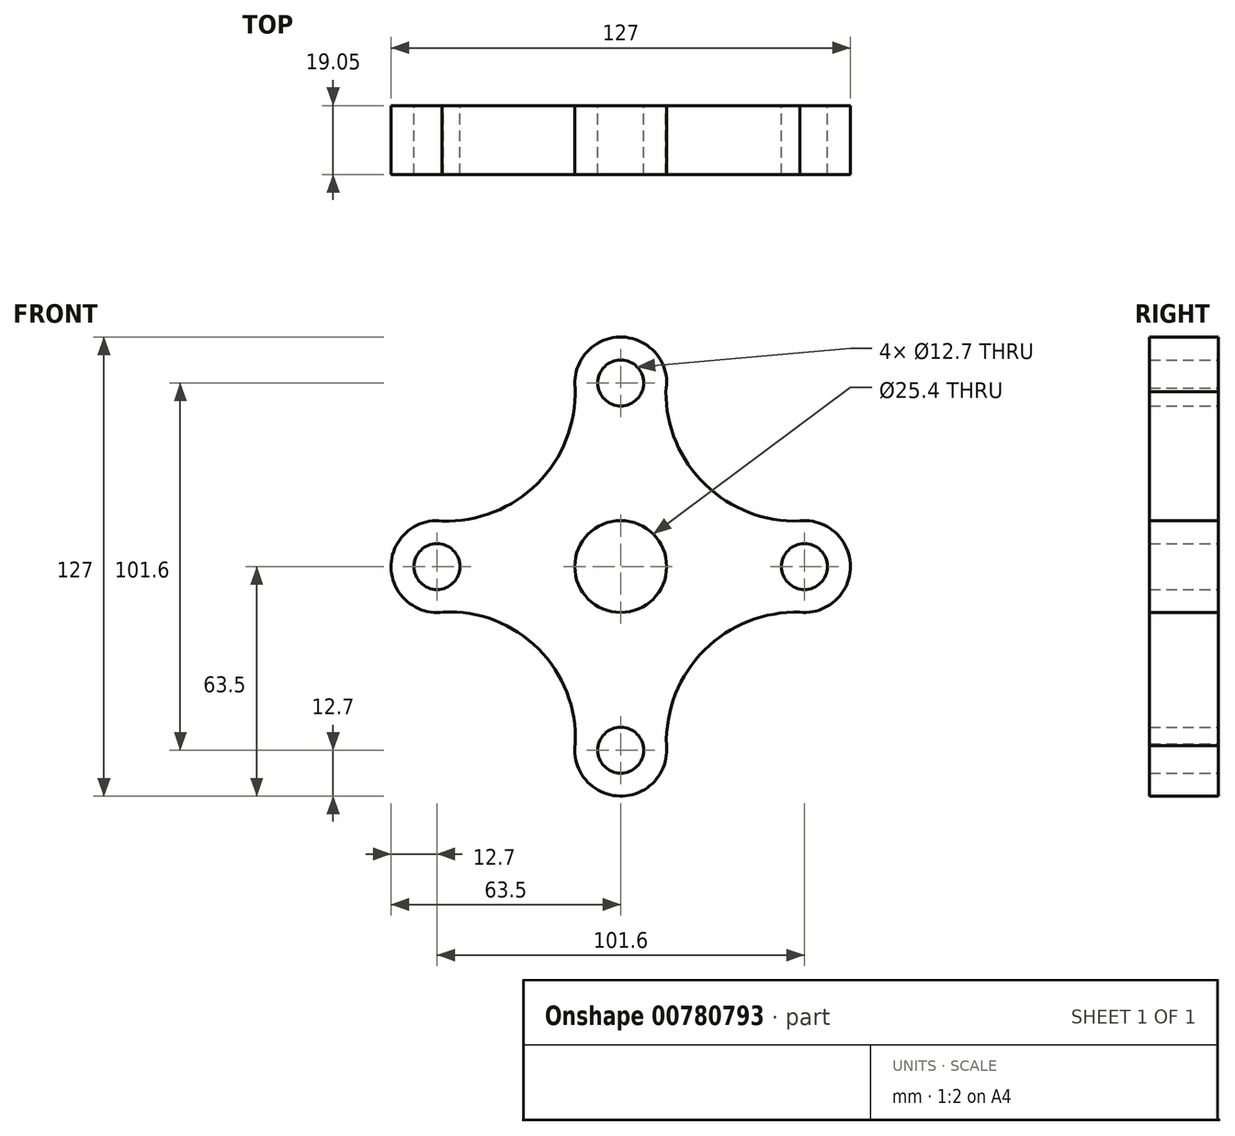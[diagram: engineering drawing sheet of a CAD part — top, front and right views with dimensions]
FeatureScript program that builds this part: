
annotation { "Feature Type Name" : "Feature", "Feature Type Description" : "" }
export const myFeature = defineFeature(function(context is Context, id is Id, definition is map)
    precondition{}
    {
        {
            var Q0;
            Q0=qCreatedBy(makeId("Front.planeOp"),FACE);
            var sketch = newSketch(context, id + "F0", { "sketchPlane" : qUnion([Q0])});
            skCircle(sketch, "E0", {"center": v(0, 0) * mm, "radius": 12.7 * mm});
            skCircle(sketch, "E1", {"center": v(0, 50.8) * mm, "radius": 6.35 * mm});
            skCircle(sketch, "E2", {"center": v(50.8, 0) * mm, "radius": 6.35 * mm});
            skCircle(sketch, "E3", {"center": v(0, -50.8) * mm, "radius": 6.35 * mm});
            skCircle(sketch, "E4", {"center": v(-50.8, 0) * mm, "radius": 6.35 * mm});
            skCircle(sketch, "E5", {"center": v(0, 50.8) * mm, "radius": 12.7 * mm});
            skCircle(sketch, "E6", {"center": v(50.8, 0) * mm, "radius": 12.7 * mm});
            skCircle(sketch, "E7", {"center": v(0, -50.8) * mm, "radius": 12.7 * mm});
            skCircle(sketch, "E8", {"center": v(-50.8, 0) * mm, "radius": 12.7 * mm});
            skPoint(sketch, "E9.end.orphan", {"position": v(54.4, -9.9) * mm});
            skPoint(sketch, "E10.orphan", {"position": v(-36.63, -9.9) * mm});
            skLineSegment(sketch, "E11", {"start": v(-50.8, 0) * mm, "end": v(-50.8, 25.3) * mm});
            skLineSegment(sketch, "E12", {"start": v(-50.8, 0) * mm, "end": v(-50.8, -21.86) * mm});
            skLineSegment(sketch, "E13", {"start": v(0, 50.8) * mm, "end": v(-22.06, 50.8) * mm});
            skLineSegment(sketch, "E14", {"start": v(0, 50.8) * mm, "end": v(25.11, 50.8) * mm});
            skLineSegment(sketch, "E15", {"start": v(50.8, 0) * mm, "end": v(50.8, 23.58) * mm});
            skLineSegment(sketch, "E16", {"start": v(50.8, 0) * mm, "end": v(50.8, -21.86) * mm});
            skLineSegment(sketch, "E17", {"start": v(0, -50.8) * mm, "end": v(-22.06, -50.8) * mm});
            skLineSegment(sketch, "E18", {"start": v(0, -50.8) * mm, "end": v(25.11, -50.8) * mm});
            skArc(sketch, "E19", {"start": v(-50.8, 12.7) * mm, "mid": v(-23.01, 23.01) * mm, "end": v(-12.7, 50.8) * mm});
            skArc(sketch, "E20", {"start": v(12.56, 50.8) * mm, "mid": v(23, 23.04) * mm, "end": v(50.8, 12.7) * mm});
            skArc(sketch, "E21", {"start": v(50.8, -12.7) * mm, "mid": v(23.11, -23.11) * mm, "end": v(12.7, -50.8) * mm});
            skArc(sketch, "E22", {"start": v(-12.7, -50.8) * mm, "mid": v(-22.75, -22.75) * mm, "end": v(-50.8, -12.7) * mm});
            skPoint(sketch, "E22.endSnap0", {"position": v(-50.8, -10.93) * mm});
            skSolve(sketch);
        }
        {
            var Q0;
            Q0 = qSketchRegion(id + "F0", true);
            extrude(context, id + "F1", {"entities" : qUnion([Q0]), "depth" : 19.05 * mm, "offsetDistance" : 25.4 * mm});
        }
    });
